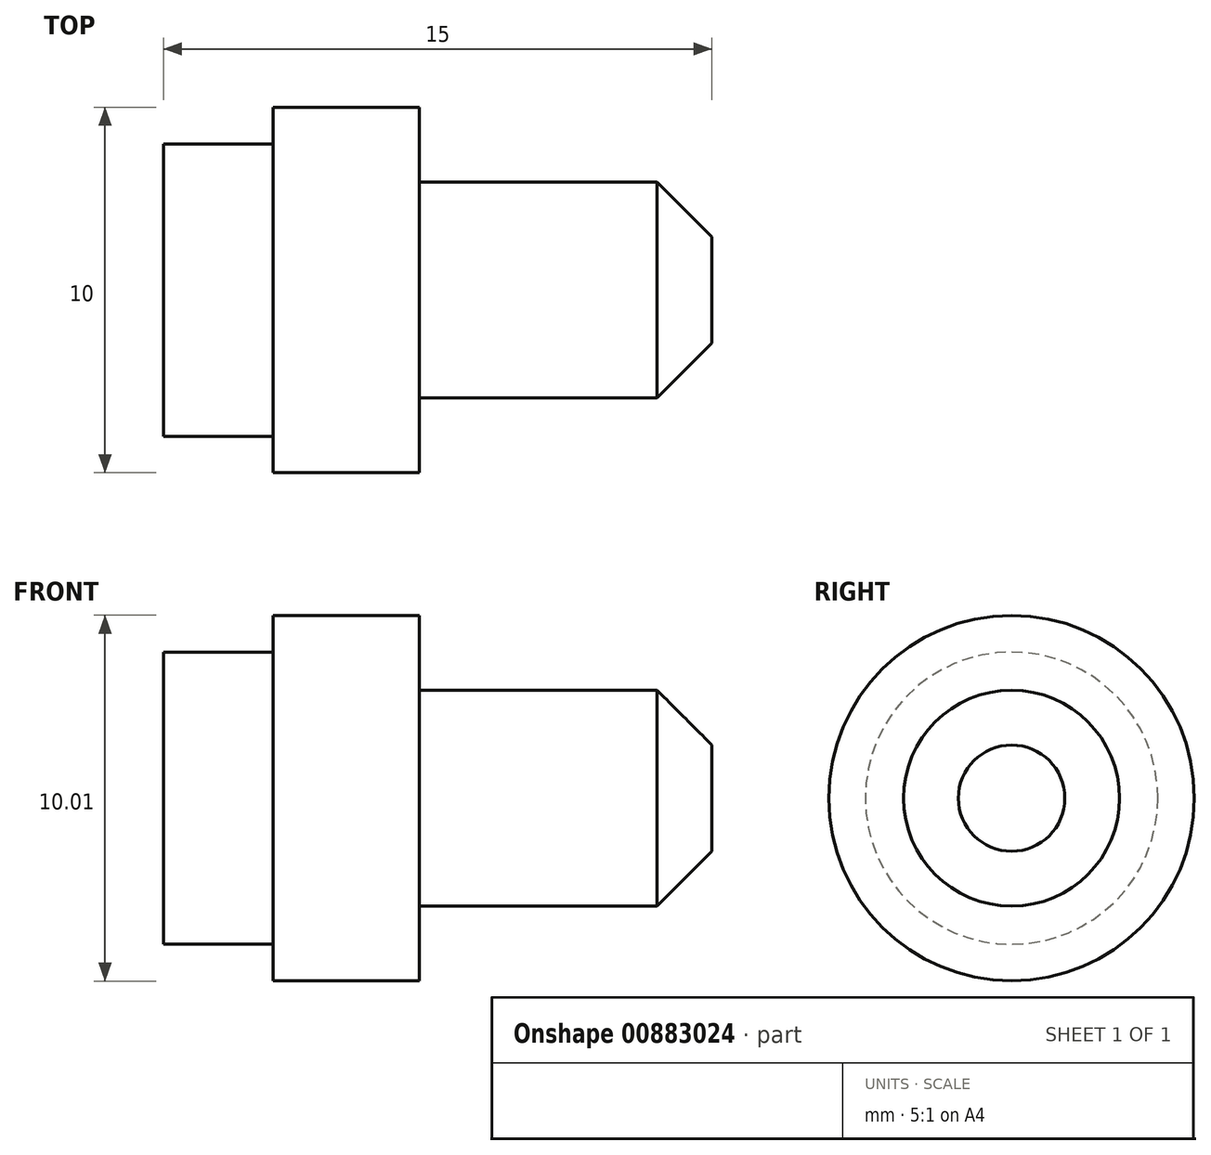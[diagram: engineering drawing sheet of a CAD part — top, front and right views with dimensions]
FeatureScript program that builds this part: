
annotation { "Feature Type Name" : "Feature", "Feature Type Description" : "" }
export const myFeature = defineFeature(function(context is Context, id is Id, definition is map)
    precondition{}
    {
        {
            var Q0;
            Q0=qCreatedBy(makeId("Front.planeOp"),FACE);
            var sketch = newSketch(context, id + "F0", { "sketchPlane" : qUnion([Q0])});
            skLineSegment(sketch, "E0", {"start": v(0, 0) * mm, "end": v(6.5, 0) * mm});
            skLineSegment(sketch, "E1", {"start": v(6.5, 0) * mm, "end": v(8, -1.5) * mm});
            skLineSegment(sketch, "E2", {"start": v(8, -1.5) * mm, "end": v(8, -2.95) * mm});
            skLineSegment(sketch, "E3", {"start": v(0, -2.96) * mm, "end": v(8, -2.96) * mm});
            skLineSegment(sketch, "E4", {"start": v(0, 0) * mm, "end": v(0, 2.05) * mm});
            skLineSegment(sketch, "E5", {"start": v(0, 2.05) * mm, "end": v(-4, 2.05) * mm});
            skLineSegment(sketch, "E6.bottom", {"start": v(-4, 2.05) * mm, "end": v(-4, 2.05) * mm});
            skLineSegment(sketch, "E6.top", {"start": v(-4, 1.05) * mm, "end": v(-4, 1.05) * mm});
            skLineSegment(sketch, "E6.left", {"start": v(-4, 2.05) * mm, "end": v(-4, 1.05) * mm});
            skLineSegment(sketch, "E6.right", {"start": v(-4, 2.05) * mm, "end": v(-4, 1.05) * mm});
            skLineSegment(sketch, "E7", {"start": v(-4, 1.05) * mm, "end": v(-7, 1.05) * mm});
            skLineSegment(sketch, "E8", {"start": v(-7, 1.05) * mm, "end": v(-7, -2.96) * mm});
            skLineSegment(sketch, "E9", {"start": v(-7, -2.96) * mm, "end": v(0, -2.96) * mm});
            skLineSegment(sketch, "E10", {"start": v(8, -2.95) * mm, "end": v(8.5, -2.95) * mm});
            skLineSegment(sketch, "E11", {"start": v(8, -1.5) * mm, "end": v(9.13, -2.63) * mm});
            skLineSegment(sketch, "E12", {"start": v(8.5, -2.95) * mm, "end": v(8.5, -2) * mm});
            skSolve(sketch);
        }
        {
            var Q0;
            Q0=makeQuery(id+"F0.imprint","IMPRINT",FACE,{"disambiguationData":[TD([[makeQuery(id+"F0.imprint","IMPRINT",EDGE,{"derivedFrom":sQuery(id+"F0.wireOp",EDGE,"E0")}),-1.0]])]});
            var Q1;
            Q1=sQuery(id+"F0.wireOp",EDGE,"E9");
            revolve(context, id + "F1", {"surfaceOperationType" : NewSurfaceOperationType.NEW, "entities" : qUnion([Q0]), "axis" : qUnion([Q1]), "revolveType" : RevolveType.FULL});
        }
    });
